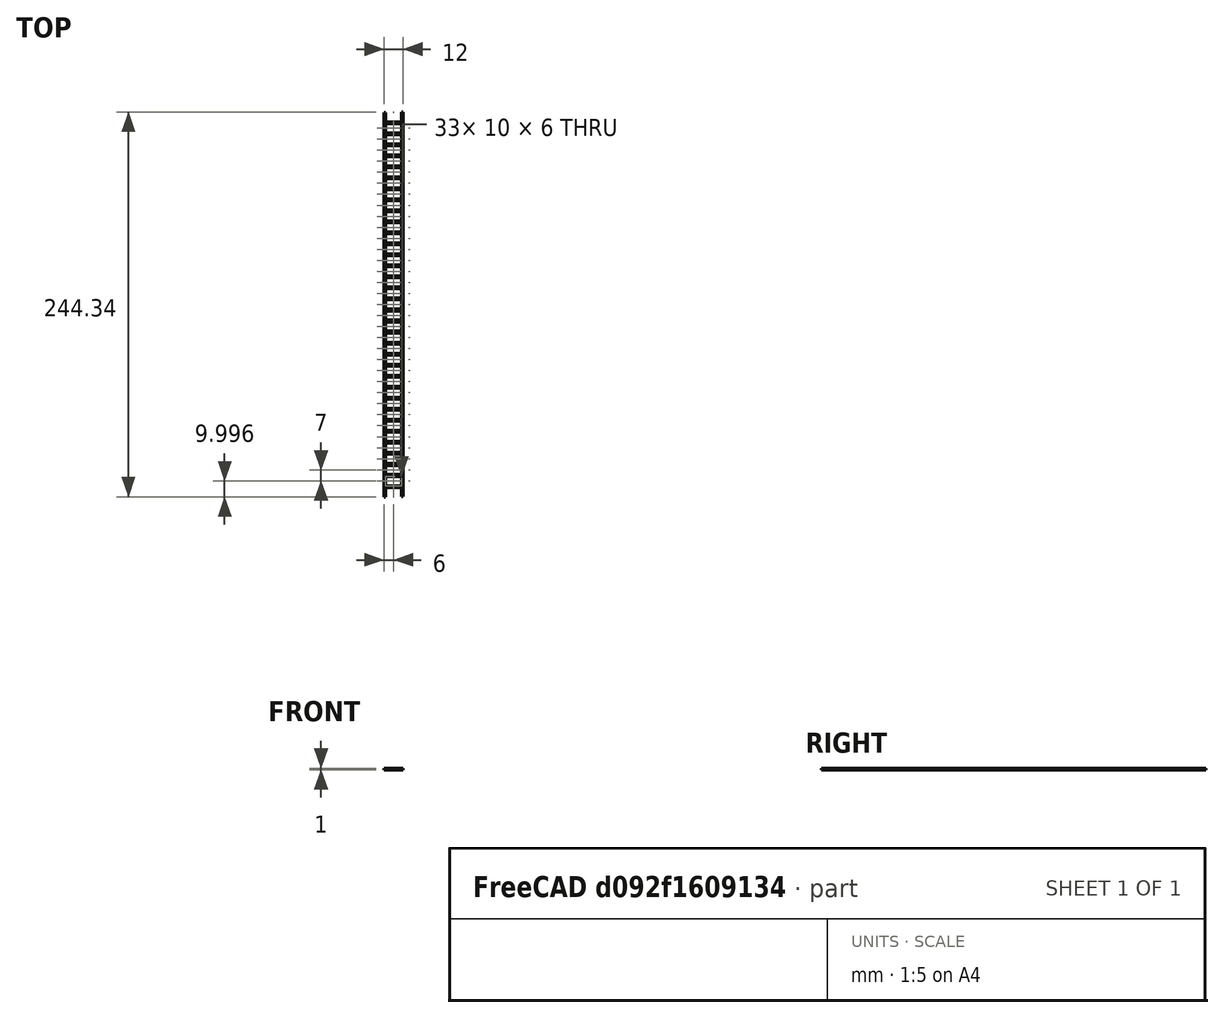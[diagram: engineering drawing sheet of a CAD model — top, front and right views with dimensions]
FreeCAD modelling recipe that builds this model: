
FCSTD DOCUMENT  (FreeCAD 1.0R39319 (Git))
Label: Ladder
License: All rights reserved
LicenseURL: http://en.wikipedia.org/wiki/All_rights_reserved
objects: Sketcher::SketchObject×2, PartDesign::Body×2, PartDesign::Pad×1
note: 9 computed .brp shape members not serialized (recipe doc carries the construction recipe); baked Part::Feature solids carry a one-line shape summary decoded from their .brp

FEATURE [Sketcher::SketchObject] Sketch
  ArcFitTolerance = 1e-06
  AttachmentSupport = -> [XY_Plane]
  FullyConstrained = true
  MakeInternals = false
  MapMode = 5
  sketch-geometry (212):
    g0: LineSegment StartX=-5 StartY=5.88621 StartZ=0 EndX=5 EndY=5.88621 EndZ=0
    g1: LineSegment StartX=-6 StartY=-0.113795 StartZ=0 EndX=-5 EndY=-0.113795 EndZ=0
    g2: LineSegment StartX=-5 StartY=5.88621 StartZ=0 EndX=-5 EndY=-0.113795 EndZ=0
    g3: LineSegment [constr] StartX=-5 StartY=6.88621 StartZ=0 EndX=-5 EndY=5.88621 EndZ=0
    g4: LineSegment StartX=5 StartY=13.8862 StartZ=0 EndX=5 EndY=19.8862 EndZ=0
    g5: LineSegment StartX=5 StartY=19.8862 StartZ=0 EndX=-5 EndY=19.8862 EndZ=0
    g6: LineSegment StartX=-5 StartY=19.8862 StartZ=0 EndX=-5 EndY=13.8862 EndZ=0
    g7: LineSegment StartX=-5 StartY=13.8862 StartZ=0 EndX=5 EndY=13.8862 EndZ=0
    g8: GeomPoint [constr] X=0 Y=16.8862 Z=0
    g9: LineSegment [constr] StartX=-5 StartY=13.8862 StartZ=0 EndX=-5 EndY=12.8862 EndZ=0
    g10: LineSegment StartX=5 StartY=21 StartZ=0 EndX=5 EndY=27 EndZ=0
    g11: LineSegment StartX=5 StartY=27 StartZ=0 EndX=-5 EndY=27 EndZ=0
    g12: LineSegment StartX=-5 StartY=27 StartZ=0 EndX=-5 EndY=21 EndZ=0
    g13: LineSegment StartX=-5 StartY=21 StartZ=0 EndX=5 EndY=21 EndZ=0
    g14: GeomPoint [constr] X=0 Y=24 Z=0
    g15: LineSegment [constr] StartX=-5 StartY=21 StartZ=0 EndX=-5 EndY=20 EndZ=0
    g16: LineSegment StartX=5 StartY=28 StartZ=0 EndX=5 EndY=34 EndZ=0
    g17: LineSegment StartX=5 StartY=34 StartZ=0 EndX=-5 EndY=34 EndZ=0
    g18: LineSegment StartX=-5 StartY=34 StartZ=0 EndX=-5 EndY=28 EndZ=0
    g19: LineSegment StartX=-5 StartY=28 StartZ=0 EndX=5 EndY=28 EndZ=0
    g20: GeomPoint [constr] X=0 Y=31 Z=0
    g21: LineSegment [constr] StartX=-5 StartY=28 StartZ=0 EndX=-5 EndY=27 EndZ=0
    g22: LineSegment StartX=5 StartY=35 StartZ=0 EndX=5 EndY=41 EndZ=0
    g23: LineSegment StartX=5 StartY=41 StartZ=0 EndX=-5 EndY=41 EndZ=0
    g24: LineSegment StartX=-5 StartY=41 StartZ=0 EndX=-5 EndY=35 EndZ=0
    g25: LineSegment StartX=-5 StartY=35 StartZ=0 EndX=5 EndY=35 EndZ=0
    g26: GeomPoint [constr] X=0 Y=38 Z=0
    g27: LineSegment [constr] StartX=-5 StartY=35 StartZ=0 EndX=-5 EndY=34 EndZ=0
    g28: LineSegment StartX=5 StartY=42 StartZ=0 EndX=5 EndY=48 EndZ=0
    g29: LineSegment StartX=5 StartY=48 StartZ=0 EndX=-5 EndY=48 EndZ=0
    g30: LineSegment StartX=-5 StartY=48 StartZ=0 EndX=-5 EndY=42 EndZ=0
    g31: LineSegment StartX=-5 StartY=42 StartZ=0 EndX=5 EndY=42 EndZ=0
    g32: GeomPoint [constr] X=0 Y=45 Z=0
    g33: LineSegment [constr] StartX=-5 StartY=42 StartZ=0 EndX=-5 EndY=41 EndZ=0
    g34: LineSegment StartX=5 StartY=49 StartZ=0 EndX=5 EndY=55 EndZ=0
    g35: LineSegment StartX=5 StartY=55 StartZ=0 EndX=-5 EndY=55 EndZ=0
    g36: LineSegment StartX=-5 StartY=55 StartZ=0 EndX=-5 EndY=49 EndZ=0
    g37: LineSegment StartX=-5 StartY=49 StartZ=0 EndX=5 EndY=49 EndZ=0
    g38: GeomPoint [constr] X=0 Y=52 Z=0
    g39: LineSegment [constr] StartX=-5 StartY=49 StartZ=0 EndX=-5 EndY=48 EndZ=0
    g40: LineSegment StartX=5 StartY=56 StartZ=0 EndX=5 EndY=62 EndZ=0
    g41: LineSegment StartX=5 StartY=62 StartZ=0 EndX=-5 EndY=62 EndZ=0
    g42: LineSegment StartX=-5 StartY=62 StartZ=0 EndX=-5 EndY=56 EndZ=0
    g43: LineSegment StartX=-5 StartY=56 StartZ=0 EndX=5 EndY=56 EndZ=0
    g44: GeomPoint [constr] X=0 Y=59 Z=0
    g45: LineSegment [constr] StartX=-5 StartY=56 StartZ=0 EndX=-5 EndY=55 EndZ=0
    g46: LineSegment StartX=5 StartY=63 StartZ=0 EndX=5 EndY=69 EndZ=0
    g47: LineSegment StartX=5 StartY=69 StartZ=0 EndX=-5 EndY=69 EndZ=0
    g48: LineSegment StartX=-5 StartY=69 StartZ=0 EndX=-5 EndY=63 EndZ=0
    g49: LineSegment StartX=-5 StartY=63 StartZ=0 EndX=5 EndY=63 EndZ=0
    g50: GeomPoint [constr] X=0 Y=66 Z=0
    g51: LineSegment [constr] StartX=-5 StartY=63 StartZ=0 EndX=-5 EndY=62 EndZ=0
    g52: LineSegment StartX=5 StartY=70 StartZ=0 EndX=5 EndY=76 EndZ=0
    g53: LineSegment StartX=5 StartY=76 StartZ=0 EndX=-5 EndY=76 EndZ=0
    g54: LineSegment StartX=-5 StartY=76 StartZ=0 EndX=-5 EndY=70 EndZ=0
    g55: LineSegment StartX=-5 StartY=70 StartZ=0 EndX=5 EndY=70 EndZ=0
    g56: GeomPoint [constr] X=0 Y=73 Z=0
    g57: LineSegment [constr] StartX=-5 StartY=70 StartZ=0 EndX=-5 EndY=69 EndZ=0
    g58: LineSegment StartX=5 StartY=77 StartZ=0 EndX=5 EndY=83 EndZ=0
    g59: LineSegment StartX=5 StartY=83 StartZ=0 EndX=-5 EndY=83 EndZ=0
    g60: LineSegment StartX=-5 StartY=83 StartZ=0 EndX=-5 EndY=77 EndZ=0
    g61: LineSegment StartX=-5 StartY=77 StartZ=0 EndX=5 EndY=77 EndZ=0
    g62: GeomPoint [constr] X=0 Y=80 Z=0
    g63: LineSegment [constr] StartX=-5 StartY=77 StartZ=0 EndX=-5 EndY=76 EndZ=0
    g64: LineSegment StartX=5 StartY=84 StartZ=0 EndX=5 EndY=90 EndZ=0
    g65: LineSegment StartX=5 StartY=90 StartZ=0 EndX=-5 EndY=90 EndZ=0
    g66: LineSegment StartX=-5 StartY=90 StartZ=0 EndX=-5 EndY=84 EndZ=0
    g67: LineSegment StartX=-5 StartY=84 StartZ=0 EndX=5 EndY=84 EndZ=0
    g68: GeomPoint [constr] X=0 Y=87 Z=0
    g69: LineSegment [constr] StartX=-5 StartY=84 StartZ=0 EndX=-5 EndY=83 EndZ=0
    g70: LineSegment StartX=5 StartY=91 StartZ=0 EndX=5 EndY=97 EndZ=0
    g71: LineSegment StartX=5 StartY=97 StartZ=0 EndX=-5 EndY=97 EndZ=0
    g72: LineSegment StartX=-5 StartY=97 StartZ=0 EndX=-5 EndY=91 EndZ=0
    g73: LineSegment StartX=-5 StartY=91 StartZ=0 EndX=5 EndY=91 EndZ=0
    g74: GeomPoint [constr] X=0 Y=94 Z=0
    g75: LineSegment [constr] StartX=-5 StartY=91 StartZ=0 EndX=-5 EndY=90 EndZ=0
    g76: LineSegment StartX=5 StartY=98 StartZ=0 EndX=5 EndY=104 EndZ=0
    g77: LineSegment StartX=5 StartY=104 StartZ=0 EndX=-5 EndY=104 EndZ=0
    g78: LineSegment StartX=-5 StartY=104 StartZ=0 EndX=-5 EndY=98 EndZ=0
    g79: LineSegment StartX=-5 StartY=98 StartZ=0 EndX=5 EndY=98 EndZ=0
    g80: GeomPoint [constr] X=0 Y=101 Z=0
    g81: LineSegment [constr] StartX=-5 StartY=98 StartZ=0 EndX=-5 EndY=97 EndZ=0
    g82: LineSegment StartX=5 StartY=105 StartZ=0 EndX=5 EndY=111 EndZ=0
    g83: LineSegment StartX=5 StartY=111 StartZ=0 EndX=-5 EndY=111 EndZ=0
    g84: LineSegment StartX=-5 StartY=111 StartZ=0 EndX=-5 EndY=105 EndZ=0
    g85: LineSegment StartX=-5 StartY=105 StartZ=0 EndX=5 EndY=105 EndZ=0
    g86: GeomPoint [constr] X=0 Y=108 Z=0
    g87: LineSegment [constr] StartX=-5 StartY=105 StartZ=0 EndX=-5 EndY=104 EndZ=0
    g88: LineSegment StartX=5 StartY=112 StartZ=0 EndX=5 EndY=118 EndZ=0
    g89: LineSegment StartX=5 StartY=118 StartZ=0 EndX=-5 EndY=118 EndZ=0
    g90: LineSegment StartX=-5 StartY=118 StartZ=0 EndX=-5 EndY=112 EndZ=0
    g91: LineSegment StartX=-5 StartY=112 StartZ=0 EndX=5 EndY=112 EndZ=0
    g92: GeomPoint [constr] X=0 Y=115 Z=0
    g93: LineSegment [constr] StartX=-5 StartY=112 StartZ=0 EndX=-5 EndY=111 EndZ=0
    g94: LineSegment StartX=5 StartY=119 StartZ=0 EndX=5 EndY=125 EndZ=0
    g95: LineSegment StartX=5 StartY=125 StartZ=0 EndX=-5 EndY=125 EndZ=0
    g96: LineSegment StartX=-5 StartY=125 StartZ=0 EndX=-5 EndY=119 EndZ=0
    g97: LineSegment StartX=-5 StartY=119 StartZ=0 EndX=5 EndY=119 EndZ=0
    g98: GeomPoint [constr] X=0 Y=122 Z=0
    g99: LineSegment [constr] StartX=-5 StartY=119 StartZ=0 EndX=-5 EndY=118 EndZ=0
    g100: LineSegment StartX=5 StartY=126 StartZ=0 EndX=5 EndY=132 EndZ=0
    g101: LineSegment StartX=5 StartY=132 StartZ=0 EndX=-5 EndY=132 EndZ=0
    g102: LineSegment StartX=-5 StartY=132 StartZ=0 EndX=-5 EndY=126 EndZ=0
    g103: LineSegment StartX=-5 StartY=126 StartZ=0 EndX=5 EndY=126 EndZ=0
    g104: GeomPoint [constr] X=0 Y=129 Z=0
    g105: LineSegment [constr] StartX=-5 StartY=126 StartZ=0 EndX=-5 EndY=125 EndZ=0
    g106: LineSegment StartX=5 StartY=133 StartZ=0 EndX=5 EndY=139 EndZ=0
    g107: LineSegment StartX=5 StartY=139 StartZ=0 EndX=-5 EndY=139 EndZ=0
    g108: LineSegment StartX=-5 StartY=139 StartZ=0 EndX=-5 EndY=133 EndZ=0
    g109: LineSegment StartX=-5 StartY=133 StartZ=0 EndX=5 EndY=133 EndZ=0
    g110: GeomPoint [constr] X=0 Y=136 Z=0
    g111: LineSegment [constr] StartX=-5 StartY=133 StartZ=0 EndX=-5 EndY=132 EndZ=0
    g112: LineSegment StartX=5 StartY=140 StartZ=0 EndX=5 EndY=146 EndZ=0
    g113: LineSegment StartX=5 StartY=146 StartZ=0 EndX=-5 EndY=146 EndZ=0
    g114: LineSegment StartX=-5 StartY=146 StartZ=0 EndX=-5 EndY=140 EndZ=0
    g115: LineSegment StartX=-5 StartY=140 StartZ=0 EndX=5 EndY=140 EndZ=0
    g116: GeomPoint [constr] X=0 Y=143 Z=0
    g117: LineSegment [constr] StartX=-5 StartY=140 StartZ=0 EndX=-5 EndY=139 EndZ=0
    g118: LineSegment StartX=5 StartY=147 StartZ=0 EndX=5 EndY=153 EndZ=0
    g119: LineSegment StartX=5 StartY=153 StartZ=0 EndX=-5 EndY=153 EndZ=0
    g120: LineSegment StartX=-5 StartY=153 StartZ=0 EndX=-5 EndY=147 EndZ=0
    g121: LineSegment StartX=-5 StartY=147 StartZ=0 EndX=5 EndY=147 EndZ=0
    g122: GeomPoint [constr] X=0 Y=150 Z=0
    g123: LineSegment [constr] StartX=-5 StartY=147 StartZ=0 EndX=-5 EndY=146 EndZ=0
    g124: LineSegment StartX=5 StartY=154 StartZ=0 EndX=5 EndY=160 EndZ=0
    g125: LineSegment StartX=5 StartY=160 StartZ=0 EndX=-5 EndY=160 EndZ=0
    g126: LineSegment StartX=-5 StartY=160 StartZ=0 EndX=-5 EndY=154 EndZ=0
    g127: LineSegment StartX=-5 StartY=154 StartZ=0 EndX=5 EndY=154 EndZ=0
    g128: GeomPoint [constr] X=0 Y=157 Z=0
    g129: LineSegment [constr] StartX=-5 StartY=154 StartZ=0 EndX=-5 EndY=153 EndZ=0
    g130: LineSegment StartX=5 StartY=161 StartZ=0 EndX=5 EndY=167 EndZ=0
    g131: LineSegment StartX=5 StartY=167 StartZ=0 EndX=-5 EndY=167 EndZ=0
    g132: LineSegment StartX=-5 StartY=167 StartZ=0 EndX=-5 EndY=161 EndZ=0
    g133: LineSegment StartX=-5 StartY=161 StartZ=0 EndX=5 EndY=161 EndZ=0
    g134: GeomPoint [constr] X=0 Y=164 Z=0
    g135: LineSegment [constr] StartX=-5 StartY=161 StartZ=0 EndX=-5 EndY=160 EndZ=0
    g136: LineSegment StartX=5 StartY=168 StartZ=0 EndX=5 EndY=174 EndZ=0
    g137: LineSegment StartX=5 StartY=174 StartZ=0 EndX=-5 EndY=174 EndZ=0
    g138: LineSegment StartX=-5 StartY=174 StartZ=0 EndX=-5 EndY=168 EndZ=0
    g139: LineSegment StartX=-5 StartY=168 StartZ=0 EndX=5 EndY=168 EndZ=0
    g140: GeomPoint [constr] X=0 Y=171 Z=0
    g141: LineSegment [constr] StartX=-5 StartY=168 StartZ=0 EndX=-5 EndY=167 EndZ=0
    g142: LineSegment StartX=5 StartY=175 StartZ=0 EndX=5 EndY=181 EndZ=0
    g143: LineSegment StartX=5 StartY=181 StartZ=0 EndX=-5 EndY=181 EndZ=0
    g144: LineSegment StartX=-5 StartY=181 StartZ=0 EndX=-5 EndY=175 EndZ=0
    g145: LineSegment StartX=-5 StartY=175 StartZ=0 EndX=5 EndY=175 EndZ=0
    g146: GeomPoint [constr] X=0 Y=178 Z=0
    g147: LineSegment [constr] StartX=-5 StartY=175 StartZ=0 EndX=-5 EndY=174 EndZ=0
    g148: LineSegment StartX=5 StartY=182 StartZ=0 EndX=5 EndY=188 EndZ=0
    g149: LineSegment StartX=5 StartY=188 StartZ=0 EndX=-5 EndY=188 EndZ=0
    g150: LineSegment StartX=-5 StartY=188 StartZ=0 EndX=-5 EndY=182 EndZ=0
    g151: LineSegment StartX=-5 StartY=182 StartZ=0 EndX=5 EndY=182 EndZ=0
    g152: GeomPoint [constr] X=0 Y=185 Z=0
    g153: LineSegment [constr] StartX=-5 StartY=182 StartZ=0 EndX=-5 EndY=181 EndZ=0
    g154: LineSegment StartX=5 StartY=189 StartZ=0 EndX=5 EndY=195 EndZ=0
    g155: LineSegment StartX=5 StartY=195 StartZ=0 EndX=-5 EndY=195 EndZ=0
    g156: LineSegment StartX=-5 StartY=195 StartZ=0 EndX=-5 EndY=189 EndZ=0
    g157: LineSegment StartX=-5 StartY=189 StartZ=0 EndX=5 EndY=189 EndZ=0
    g158: GeomPoint [constr] X=0 Y=192 Z=0
    g159: LineSegment [constr] StartX=-5 StartY=189 StartZ=0 EndX=-5 EndY=188 EndZ=0
    g160: LineSegment StartX=5 StartY=196 StartZ=0 EndX=5 EndY=202 EndZ=0
    g161: LineSegment StartX=5 StartY=202 StartZ=0 EndX=-5 EndY=202 EndZ=0
    g162: LineSegment StartX=-5 StartY=202 StartZ=0 EndX=-5 EndY=196 EndZ=0
    g163: LineSegment StartX=-5 StartY=196 StartZ=0 EndX=5 EndY=196 EndZ=0
    g164: GeomPoint [constr] X=0 Y=199 Z=0
    g165: LineSegment [constr] StartX=-5 StartY=196 StartZ=0 EndX=-5 EndY=195 EndZ=0
    g166: LineSegment StartX=5 StartY=203 StartZ=0 EndX=5 EndY=209 EndZ=0
    g167: LineSegment StartX=5 StartY=209 StartZ=0 EndX=-5 EndY=209 EndZ=0
    g168: LineSegment StartX=-5 StartY=209 StartZ=0 EndX=-5 EndY=203 EndZ=0
    g169: LineSegment StartX=-5 StartY=203 StartZ=0 EndX=5 EndY=203 EndZ=0
    g170: GeomPoint [constr] X=0 Y=206 Z=0
    g171: LineSegment [constr] StartX=-5 StartY=203 StartZ=0 EndX=-5 EndY=202 EndZ=0
    g172: LineSegment StartX=5 StartY=210 StartZ=0 EndX=5 EndY=216 EndZ=0
    g173: LineSegment StartX=5 StartY=216 StartZ=0 EndX=-5 EndY=216 EndZ=0
    g174: LineSegment StartX=-5 StartY=216 StartZ=0 EndX=-5 EndY=210 EndZ=0
    g175: LineSegment StartX=-5 StartY=210 StartZ=0 EndX=5 EndY=210 EndZ=0
    g176: GeomPoint [constr] X=0 Y=213 Z=0
    g177: LineSegment [constr] StartX=-5 StartY=210 StartZ=0 EndX=-5 EndY=209 EndZ=0
    g178: LineSegment StartX=5 StartY=217 StartZ=0 EndX=5 EndY=223 EndZ=0
    g179: LineSegment StartX=5 StartY=223 StartZ=0 EndX=-5 EndY=223 EndZ=0
    g180: LineSegment StartX=-5 StartY=223 StartZ=0 EndX=-5 EndY=217 EndZ=0
    g181: LineSegment StartX=-5 StartY=217 StartZ=0 EndX=5 EndY=217 EndZ=0
    g182: GeomPoint [constr] X=0 Y=220 Z=0
    g183: LineSegment [constr] StartX=-5 StartY=217 StartZ=0 EndX=-5 EndY=216 EndZ=0
    g184: LineSegment StartX=5 StartY=224 StartZ=0 EndX=5 EndY=230 EndZ=0
    g185: LineSegment StartX=5 StartY=230 StartZ=0 EndX=-5 EndY=230 EndZ=0
    g186: LineSegment StartX=-5 StartY=230 StartZ=0 EndX=-5 EndY=224 EndZ=0
    g187: LineSegment StartX=-5 StartY=224 StartZ=0 EndX=5 EndY=224 EndZ=0
    g188: GeomPoint [constr] X=0 Y=227 Z=0
    g189: LineSegment [constr] StartX=-5 StartY=224 StartZ=0 EndX=-5 EndY=223 EndZ=0
    g190: LineSegment StartX=5 StartY=231 StartZ=0 EndX=5 EndY=237 EndZ=0
    g191: LineSegment StartX=5 StartY=237 StartZ=0 EndX=-5 EndY=237 EndZ=0
    g192: LineSegment StartX=-5 StartY=237 StartZ=0 EndX=-5 EndY=231 EndZ=0
    g193: LineSegment StartX=-5 StartY=231 StartZ=0 EndX=5 EndY=231 EndZ=0
    g194: GeomPoint [constr] X=0 Y=234 Z=0
    g195: LineSegment [constr] StartX=-5 StartY=231 StartZ=0 EndX=-5 EndY=230 EndZ=0
    g196: LineSegment StartX=5 StartY=238 StartZ=0 EndX=5 EndY=244.228 EndZ=0
    g197: LineSegment StartX=-5 StartY=244 StartZ=0 EndX=-5 EndY=238 EndZ=0
    g198: LineSegment StartX=-5 StartY=238 StartZ=0 EndX=5 EndY=238 EndZ=0
    g199: GeomPoint [constr] X=1.09e-14 Y=241 Z=0
    g200: LineSegment [constr] StartX=-5 StartY=238 StartZ=0 EndX=-5 EndY=237 EndZ=0
    g201: LineSegment StartX=-6 StartY=244 StartZ=0 EndX=-5 EndY=244 EndZ=0
    g202: LineSegment StartX=5 StartY=244.228 StartZ=0 EndX=6 EndY=244.228 EndZ=0
    g203: LineSegment StartX=6 StartY=244.228 StartZ=0 EndX=6 EndY=0.113795 EndZ=0
    g204: LineSegment StartX=5 StartY=5.88621 StartZ=0 EndX=5 EndY=0.113795 EndZ=0
    g205: LineSegment StartX=5 StartY=0.113795 StartZ=0 EndX=6 EndY=0.113795 EndZ=0
    g206: LineSegment StartX=-5 StartY=6.88621 StartZ=0 EndX=5 EndY=6.88621 EndZ=0
    g207: LineSegment StartX=5 StartY=6.88621 StartZ=0 EndX=5 EndY=12.8862 EndZ=0
    g208: LineSegment StartX=5 StartY=12.8862 StartZ=0 EndX=-5 EndY=12.8862 EndZ=0
    g209: LineSegment StartX=-5 StartY=12.8862 StartZ=0 EndX=-5 EndY=6.88621 EndZ=0
    g210: GeomPoint [constr] X=0 Y=9.88621 Z=0
    g211: LineSegment StartX=-6 StartY=244 StartZ=0 EndX=-6 EndY=-0.113795 EndZ=0
  constraints (631):
    c: Horizontal(g0)
    c: DistanceY(g1,g0) = 6
    c: DistanceX(g0,g0) = 10
    c: DistanceX(g1,g1) = 1
    c: Coincident(g2,g0)
    c: Coincident(g3,g0)
    c: DistanceY(g3,g3) = 1
    c: Coincident(g1,g2)
    c: Vertical(g2)
    c: Horizontal(g1)
    c: Coincident(g4,g5)
    c: Coincident(g10,g11)
    c: Coincident(g16,g17)
    c: Coincident(g22,g23)
    c: Coincident(g28,g29)
    c: Coincident(g34,g35)
    c: Coincident(g40,g41)
    c: Coincident(g46,g47)
    c: Coincident(g52,g53)
    c: Coincident(g58,g59)
    c: Coincident(g64,g65)
    c: Coincident(g70,g71)
    c: Coincident(g76,g77)
    c: Coincident(g82,g83)
    c: Coincident(g88,g89)
    c: Coincident(g94,g95)
    c: Coincident(g100,g101)
    c: Coincident(g106,g107)
    c: Coincident(g112,g113)
    c: Coincident(g118,g119)
    c: Coincident(g124,g125)
    c: Coincident(g130,g131)
    c: Coincident(g136,g137)
    c: Coincident(g142,g143)
    c: Coincident(g148,g149)
    c: Coincident(g154,g155)
    c: Coincident(g160,g161)
    c: Coincident(g166,g167)
    c: Coincident(g172,g173)
    c: Coincident(g178,g179)
    c: Coincident(g5,g6)
    c: Coincident(g11,g12)
    c: Coincident(g17,g18)
    c: Coincident(g23,g24)
    c: Coincident(g29,g30)
    c: Coincident(g35,g36)
    c: Coincident(g41,g42)
    c: Coincident(g47,g48)
    c: Coincident(g53,g54)
    c: Coincident(g59,g60)
    c: Coincident(g65,g66)
    c: Coincident(g71,g72)
    c: Coincident(g77,g78)
    c: Coincident(g83,g84)
    c: Coincident(g89,g90)
    c: Coincident(g95,g96)
    c: Coincident(g101,g102)
    c: Coincident(g107,g108)
    c: Coincident(g113,g114)
    c: Coincident(g119,g120)
    c: Coincident(g125,g126)
    c: Coincident(g131,g132)
    c: Coincident(g137,g138)
    c: Coincident(g143,g144)
    c: Coincident(g149,g150)
    c: Coincident(g155,g156)
    c: Coincident(g161,g162)
    c: Coincident(g167,g168)
    c: Coincident(g173,g174)
    c: Coincident(g179,g180)
    c: Coincident(g6,g7)
    c: Coincident(g12,g13)
    c: Coincident(g18,g19)
    c: Coincident(g24,g25)
    c: Coincident(g30,g31)
    c: Coincident(g36,g37)
    c: Coincident(g42,g43)
    c: Coincident(g48,g49)
    c: Coincident(g54,g55)
    c: Coincident(g60,g61)
    c: Coincident(g66,g67)
    c: Coincident(g72,g73)
    c: Coincident(g78,g79)
    c: Coincident(g84,g85)
    c: Coincident(g90,g91)
    c: Coincident(g96,g97)
    c: Coincident(g102,g103)
    c: Coincident(g108,g109)
    c: Coincident(g114,g115)
    c: Coincident(g120,g121)
    c: Coincident(g126,g127)
    c: Coincident(g132,g133)
    c: Coincident(g138,g139)
    c: Coincident(g144,g145)
    c: Coincident(g150,g151)
    c: Coincident(g156,g157)
    c: Coincident(g162,g163)
    c: Coincident(g168,g169)
    c: Coincident(g174,g175)
    c: Coincident(g180,g181)
    c: Coincident(g7,g4)
    c: Coincident(g13,g10)
    c: Coincident(g19,g16)
    c: Coincident(g25,g22)
    c: Coincident(g31,g28)
    c: Coincident(g37,g34)
    c: Coincident(g43,g40)
    c: Coincident(g49,g46)
    c: Coincident(g55,g52)
    c: Coincident(g61,g58)
    c: Coincident(g67,g64)
    c: Coincident(g73,g70)
    c: Coincident(g79,g76)
    c: Coincident(g85,g82)
    c: Coincident(g91,g88)
    c: Coincident(g97,g94)
    c: Coincident(g103,g100)
    c: Coincident(g109,g106)
    c: Coincident(g115,g112)
    c: Coincident(g121,g118)
    c: Coincident(g127,g124)
    c: Coincident(g133,g130)
    c: Coincident(g139,g136)
    c: Coincident(g145,g142)
    c: Coincident(g151,g148)
    c: Coincident(g157,g154)
    c: Coincident(g163,g160)
    c: Coincident(g169,g166)
    c: Coincident(g175,g172)
    c: Coincident(g181,g178)
    c: Vertical(g4)
    c: Vertical(g10)
    c: Vertical(g16)
    c: Vertical(g22)
    c: Vertical(g28)
    c: Vertical(g34)
    c: Vertical(g40)
    c: Vertical(g46)
    c: Vertical(g52)
    c: Vertical(g58)
    c: Vertical(g64)
    c: Vertical(g70)
    c: Vertical(g76)
    c: Vertical(g82)
    c: Vertical(g88)
    c: Vertical(g94)
    c: Vertical(g100)
    c: Vertical(g106)
    c: Vertical(g112)
    c: Vertical(g118)
    c: Vertical(g124)
    c: Vertical(g130)
    c: Vertical(g136)
    c: Vertical(g142)
    c: Vertical(g148)
    c: Vertical(g154)
    c: Vertical(g160)
    c: Vertical(g166)
    c: Vertical(g172)
    c: Vertical(g178)
    c: Vertical(g6)
    c: Vertical(g12)
    c: Vertical(g18)
    c: Vertical(g24)
    c: Vertical(g30)
    c: Vertical(g36)
    c: Vertical(g42)
    c: Vertical(g48)
    c: Vertical(g54)
    c: Vertical(g60)
    c: Vertical(g66)
    c: Vertical(g72)
    c: Vertical(g78)
    c: Vertical(g84)
    c: Vertical(g90)
    c: Vertical(g96)
    c: Vertical(g102)
    c: Vertical(g108)
    c: Vertical(g114)
    c: Vertical(g120)
    c: Vertical(g126)
    c: Vertical(g132)
    c: Vertical(g138)
    c: Vertical(g144)
    c: Vertical(g150)
    c: Vertical(g156)
    c: Vertical(g162)
    c: Vertical(g168)
    c: Vertical(g174)
    c: Vertical(g180)
    c: Horizontal(g5)
    c: Horizontal(g11)
    c: Horizontal(g17)
    c: Horizontal(g23)
    c: Horizontal(g29)
    c: Horizontal(g35)
    c: Horizontal(g41)
    c: Horizontal(g47)
    c: Horizontal(g53)
    c: Horizontal(g59)
    c: Horizontal(g65)
    c: Horizontal(g71)
    c: Horizontal(g77)
    c: Horizontal(g83)
    c: Horizontal(g89)
    c: Horizontal(g95)
    c: Horizontal(g101)
    c: Horizontal(g107)
    c: Horizontal(g113)
    c: Horizontal(g119)
    c: Horizontal(g125)
    c: Horizontal(g131)
    c: Horizontal(g137)
    c: Horizontal(g143)
    c: Horizontal(g149)
    c: Horizontal(g155)
    c: Horizontal(g161)
    c: Horizontal(g167)
    c: Horizontal(g173)
    c: Horizontal(g179)
    c: Horizontal(g7)
    c: Horizontal(g13)
    c: Horizontal(g19)
    c: Horizontal(g25)
    c: Horizontal(g31)
    c: Horizontal(g37)
    c: Horizontal(g43)
    c: Horizontal(g49)
    c: Horizontal(g55)
    c: Horizontal(g61)
    c: Horizontal(g67)
    c: Horizontal(g73)
    c: Horizontal(g79)
    c: Horizontal(g85)
    c: Horizontal(g91)
    c: Horizontal(g97)
    c: Horizontal(g103)
    c: Horizontal(g109)
    c: Horizontal(g115)
    c: Horizontal(g121)
    c: Horizontal(g127)
    c: Horizontal(g133)
    c: Horizontal(g139)
    c: Horizontal(g145)
    c: Horizontal(g151)
    c: Horizontal(g157)
    c: Horizontal(g163)
    c: Horizontal(g169)
    c: Horizontal(g175)
    c: Horizontal(g181)
    c: Symmetric(g6,g4,g8)
    c: Symmetric(g12,g10,g14)
    c: Symmetric(g18,g16,g20)
    c: Symmetric(g24,g22,g26)
    c: Symmetric(g30,g28,g32)
    c: Symmetric(g36,g34,g38)
    c: Symmetric(g42,g40,g44)
    c: Symmetric(g48,g46,g50)
    c: Symmetric(g54,g52,g56)
    c: Symmetric(g60,g58,g62)
    c: Symmetric(g66,g64,g68)
    c: Symmetric(g72,g70,g74)
    c: Symmetric(g78,g76,g80)
    c: Symmetric(g84,g82,g86)
    c: Symmetric(g90,g88,g92)
    c: Symmetric(g96,g94,g98)
    c: Symmetric(g102,g100,g104)
    c: Symmetric(g108,g106,g110)
    c: Symmetric(g114,g112,g116)
    c: Symmetric(g120,g118,g122)
    c: Symmetric(g126,g124,g128)
    c: Symmetric(g132,g130,g134)
    c: Symmetric(g138,g136,g140)
    c: Symmetric(g144,g142,g146)
    c: Symmetric(g150,g148,g152)
    c: Symmetric(g156,g154,g158)
    c: Symmetric(g162,g160,g164)
    c: Symmetric(g168,g166,g170)
    c: Symmetric(g174,g172,g176)
    c: Symmetric(g180,g178,g182)
    c: DistanceY(g6,g6) = 6
    c: DistanceY(g12,g12) = 6
    c: DistanceY(g18,g18) = 6
    c: DistanceY(g24,g24) = 6
    c: DistanceY(g30,g30) = 6
    c: DistanceY(g36,g36) = 6
    c: DistanceY(g42,g42) = 6
    c: DistanceY(g48,g48) = 6
    c: DistanceY(g54,g54) = 6
    c: DistanceY(g60,g60) = 6
    c: DistanceY(g66,g66) = 6
    c: DistanceY(g72,g72) = 6
    c: DistanceY(g78,g78) = 6
    c: DistanceY(g84,g84) = 6
    c: DistanceY(g90,g90) = 6
    c: DistanceY(g96,g96) = 6
    c: DistanceY(g102,g102) = 6
    c: DistanceY(g108,g108) = 6
    c: DistanceY(g114,g114) = 6
    c: DistanceY(g120,g120) = 6
    c: DistanceY(g126,g126) = 6
    c: DistanceY(g132,g132) = 6
    c: DistanceY(g138,g138) = 6
    c: DistanceY(g144,g144) = 6
    c: DistanceY(g150,g150) = 6
    c: DistanceY(g156,g156) = 6
    c: DistanceY(g162,g162) = 6
    c: DistanceY(g168,g168) = 6
    c: DistanceY(g174,g174) = 6
    c: DistanceY(g180,g180) = 6
    c: Coincident(g9,g6)
    c: Coincident(g15,g12)
    c: Coincident(g21,g18)
    c: Coincident(g27,g24)
    c: Coincident(g33,g30)
    c: Coincident(g39,g36)
    c: Coincident(g45,g42)
    c: Coincident(g51,g48)
    c: Coincident(g57,g54)
    c: Coincident(g63,g60)
    c: Coincident(g69,g66)
    c: Coincident(g75,g72)
    c: Coincident(g81,g78)
    c: Coincident(g87,g84)
    c: Coincident(g93,g90)
    c: Coincident(g99,g96)
    c: Coincident(g105,g102)
    c: Coincident(g111,g108)
    c: Coincident(g117,g114)
    c: Coincident(g123,g120)
    c: Coincident(g129,g126)
    c: Coincident(g135,g132)
    c: Coincident(g141,g138)
    c: Coincident(g147,g144)
    c: Coincident(g153,g150)
    c: Coincident(g159,g156)
    c: Coincident(g165,g162)
    c: Coincident(g171,g168)
    c: Coincident(g177,g174)
    c: Coincident(g183,g180)
    c: DistanceX(g5,g5) = 10
    c: DistanceX(g11,g11) = 10
    c: DistanceX(g17,g17) = 10
    c: DistanceX(g23,g23) = 10
    c: DistanceX(g29,g29) = 10
    c: DistanceX(g35,g35) = 10
    c: DistanceX(g41,g41) = 10
    c: DistanceX(g47,g47) = 10
    c: DistanceX(g53,g53) = 10
    c: DistanceX(g59,g59) = 10
    c: DistanceX(g65,g65) = 10
    c: DistanceX(g71,g71) = 10
    c: DistanceX(g77,g77) = 10
    c: DistanceX(g83,g83) = 10
    c: DistanceX(g89,g89) = 10
    c: DistanceX(g95,g95) = 10
    c: DistanceX(g101,g101) = 10
    c: DistanceX(g107,g107) = 10
    c: DistanceX(g113,g113) = 10
    c: DistanceX(g119,g119) = 10
    c: DistanceX(g125,g125) = 10
    c: DistanceX(g131,g131) = 10
    c: DistanceX(g137,g137) = 10
    c: DistanceX(g143,g143) = 10
    c: DistanceX(g149,g149) = 10
    c: DistanceX(g155,g155) = 10
    c: DistanceX(g161,g161) = 10
    c: DistanceX(g167,g167) = 10
    c: DistanceX(g173,g173) = 10
    c: DistanceX(g179,g179) = 10
    c: DistanceY(g9,g9) = 1
    c: DistanceY(g15,g15) = 1
    c: DistanceY(g21,g21) = 1
    c: DistanceY(g27,g27) = 1
    c: DistanceY(g33,g33) = 1
    c: DistanceY(g39,g39) = 1
    c: DistanceY(g45,g45) = 1
    c: DistanceY(g51,g51) = 1
    c: DistanceY(g57,g57) = 1
    c: DistanceY(g63,g63) = 1
    c: DistanceY(g69,g69) = 1
    c: DistanceY(g75,g75) = 1
    c: DistanceY(g81,g81) = 1
    c: DistanceY(g87,g87) = 1
    c: DistanceY(g93,g93) = 1
    c: DistanceY(g99,g99) = 1
    c: DistanceY(g105,g105) = 1
    c: DistanceY(g111,g111) = 1
    c: DistanceY(g117,g117) = 1
    c: DistanceY(g123,g123) = 1
    c: DistanceY(g129,g129) = 1
    c: DistanceY(g135,g135) = 1
    c: DistanceY(g141,g141) = 1
    c: DistanceY(g147,g147) = 1
    c: DistanceY(g153,g153) = 1
    c: DistanceY(g159,g159) = 1
    c: DistanceY(g165,g165) = 1
    c: DistanceY(g171,g171) = 1
    c: DistanceY(g177,g177) = 1
    c: DistanceY(g183,g183) = 1
    c: Block(g5)
    c: Block(g11)
    c: Block(g17)
    c: Block(g23)
    c: Block(g29)
    c: Block(g35)
    c: Block(g41)
    c: Block(g47)
    c: Block(g53)
    c: Block(g59)
    c: Block(g65)
    c: Block(g71)
    c: Block(g77)
    c: Block(g83)
    c: Block(g89)
    c: Block(g95)
    c: Block(g101)
    c: Block(g107)
    c: Block(g113)
    c: Block(g119)
    c: Block(g125)
    c: Block(g131)
    c: Block(g137)
    c: Block(g143)
    c: Block(g149)
    c: Block(g155)
    c: Block(g161)
    c: Block(g167)
    c: Block(g173)
    c: Block(g179)
    c: Block(g6)
    c: Block(g12)
    c: Block(g18)
    c: Block(g24)
    c: Block(g30)
    c: Block(g36)
    c: Block(g42)
    c: Block(g48)
    c: Block(g54)
    c: Block(g60)
    c: Block(g66)
    c: Block(g72)
    c: Block(g78)
    c: Block(g84)
    c: Block(g90)
    c: Block(g96)
    c: Block(g102)
    c: Block(g108)
    c: Block(g114)
    c: Block(g120)
    c: Block(g126)
    c: Block(g132)
    c: Block(g138)
    c: Block(g144)
    c: Block(g150)
    c: Block(g156)
    c: Block(g162)
    c: Block(g168)
    c: Block(g174)
    c: Block(g180)
    c: Block(g7)
    c: Block(g13)
    c: Block(g19)
    c: Block(g25)
    c: Block(g31)
    c: Block(g37)
    c: Block(g43)
    c: Block(g49)
    c: Block(g55)
    c: Block(g61)
    c: Block(g67)
    c: Block(g73)
    c: Block(g79)
    c: Block(g85)
    c: Block(g91)
    c: Block(g97)
    c: Block(g103)
    c: Block(g109)
    c: Block(g115)
    c: Block(g121)
    c: Block(g127)
    c: Block(g133)
    c: Block(g139)
    c: Block(g145)
    c: Block(g151)
    c: Block(g157)
    c: Block(g163)
    c: Block(g169)
    c: Block(g175)
    c: Block(g181)
    c: Block(g4)
    c: Block(g10)
    c: Block(g16)
    c: Block(g22)
    c: Block(g28)
    c: Block(g34)
    c: Block(g40)
    c: Block(g46)
    c: Block(g52)
    c: Block(g58)
    c: Block(g64)
    c: Block(g70)
    c: Block(g76)
    c: Block(g82)
    c: Block(g88)
    c: Block(g94)
    c: Block(g100)
    c: Block(g106)
    c: Block(g112)
    c: Block(g118)
    c: Block(g124)
    c: Block(g130)
    c: Block(g136)
    c: Block(g142)
    c: Block(g148)
    c: Block(g154)
    c: Block(g160)
    c: Block(g166)
    c: Block(g172)
    c: Block(g178)
    c: Block(g9)
    c: Block(g15)
    c: Block(g21)
    c: Block(g27)
    c: Block(g33)
    c: Block(g39)
    c: Block(g45)
    c: Block(g51)
    c: Block(g57)
    c: Block(g63)
    c: Block(g69)
    c: Block(g75)
    c: Block(g81)
    c: Block(g87)
    c: Block(g93)
    c: Block(g99)
    c: Block(g105)
    c: Block(g111)
    c: Block(g117)
    c: Block(g123)
    c: Block(g129)
    c: Block(g135)
    c: Block(g141)
    c: Block(g147)
    c: Block(g153)
    c: Block(g159)
    c: Block(g165)
    c: Block(g171)
    c: Block(g177)
    c: Block(g183)
    c: Coincident(g184,g185)
    c: Coincident(g190,g191)
    c: Coincident(g185,g186)
    c: Coincident(g191,g192)
    c: Coincident(g186,g187)
    c: Coincident(g192,g193)
    c: Coincident(g197,g198)
    c: Coincident(g187,g184)
    c: Coincident(g193,g190)
    c: Coincident(g198,g196)
    c: Vertical(g184)
    c: Vertical(g190)
    c: Vertical(g196)
    c: Vertical(g186)
    c: Vertical(g192)
    c: Vertical(g197)
    c: Horizontal(g185)
    c: Horizontal(g191)
    c: Horizontal(g187)
    c: Horizontal(g193)
    c: Horizontal(g198)
    c: Symmetric(g186,g184,g188)
    c: Symmetric(g192,g190,g194)
    c: Symmetric(g197,g196,g199)
    c: DistanceY(g186,g186) = 6
    c: DistanceY(g192,g192) = 6
    c: DistanceY(g197,g197) = 6
    c: Coincident(g189,g186)
    c: Coincident(g195,g192)
    c: Coincident(g200,g197)
    c: DistanceX(g185,g185) = 10
    c: DistanceX(g191,g191) = 10
    c: DistanceX(g197,g196) = 10
    c: DistanceY(g189,g189) = 1
    c: DistanceY(g195,g195) = 1
    c: DistanceY(g200,g200) = 1
    c: Block(g185)
    c: Block(g191)
    c: Block(g186)
    c: Block(g192)
    c: Block(g197)
    c: Block(g187)
    c: Block(g193)
    c: Block(g198)
    c: Block(g184)
    c: Block(g190)
    c: Block(g196)
    c: Block(g189)
    c: Block(g195)
    c: Block(g200)
    c: Coincident(g201,g197)
    c: Horizontal(g201)
    c: Coincident(g196,g202)
    c: Horizontal(g202)
    c: Coincident(g202,g203)
    c: Vertical(g203)
    c: Equal(g202,g201)
    c: Coincident(g0,g204)
    c: Coincident(g204,g205)
    c: Coincident(g205,g203)
    c: Horizontal(g205)
    c: Vertical(g204)
    c: Coincident(g206,g207)
    c: Coincident(g207,g208)
    c: Coincident(g208,g209)
    c: Coincident(g209,g206)
    c: Horizontal(g206)
    c: Horizontal(g208)
    c: Vertical(g207)
    c: Vertical(g209)
    c: Symmetric(g208,g206,g210)
    c: PointOnObject(g210,g-2)
    c: Equal(g208,g7)
    c: Equal(g4,g207)
    c: Coincident(g208,g9)
    c: Coincident(g3,g206)
    c: Symmetric(g204,g1,g-1)
    c: Vertical(g211)
    c: Equal(g211,g203)
    c: Coincident(g211,g1)
    c: Coincident(g211,g201)
FEATURE [PartDesign::Pad] Pad
  Direction = (0,0,1)
  Length = 1
  Length2 = 10
  Profile = -> Sketch
  ReferenceAxis = -> Sketch [N_Axis]
  Refine = true
  Suppressed = false
  Type = 0
FEATURE [PartDesign::Body] Body
  AllowCompound = true
  Group = -> [Sketch,Pad]
  Origin = -> Origin
  Tip = -> Pad
FEATURE [Sketcher::SketchObject] Sketch001
  ArcFitTolerance = 1e-06
  AttachmentSupport = -> [XY_Plane001]
  FullyConstrained = false
  MakeInternals = false
  MapMode = 5
  sketch-geometry (11):
    g0: LineSegment StartX=-37.6711 StartY=0 StartZ=0 EndX=37.6711 EndY=0 EndZ=0
    g1: LineSegment StartX=37.6711 StartY=0 StartZ=0 EndX=22.7716 EndY=181.451 EndZ=0
    g2: LineSegment StartX=22.7716 StartY=181.451 StartZ=0 EndX=-22.7716 EndY=181.451 EndZ=0
    g3: LineSegment StartX=-22.7716 StartY=181.451 StartZ=0 EndX=-37.6711 EndY=0 EndZ=0
    g4: GeomPoint [constr] X=0 Y=101.553 Z=0
    g5: LineSegment StartX=21.7004 StartY=23.9757 StartZ=0 EndX=-14.7224 EndY=47.0077 EndZ=0
    g6: LineSegment StartX=-14.7224 StartY=47.0077 StartZ=0 EndX=12.3269 EndY=62.2732 EndZ=0
    g7: LineSegment StartX=12.3269 StartY=62.2732 StartZ=0 EndX=-17.9362 EndY=82.8949 EndZ=0
    g8: LineSegment StartX=-17.9362 StartY=82.8949 StartZ=0 EndX=15.5406 EndY=105.124 EndZ=0
    g9: LineSegment StartX=15.5406 StartY=105.124 StartZ=0 EndX=-10.7052 EndY=124.674 EndZ=0
    g10: LineSegment StartX=-10.7052 StartY=124.674 StartZ=0 EndX=12.059 EndY=140.743 EndZ=0
  constraints (13):
    c: Coincident(g0,g1)
    c: Coincident(g1,g2)
    c: Coincident(g2,g3)
    c: Coincident(g3,g0)
    c: Horizontal(g0)
    c: PointOnObject(g4,g-2)
    c: Symmetric(g0,g0,g-1)
    c: Symmetric(g1,g2,g-2)
    c: Coincident(g5,g6)
    c: Coincident(g6,g7)
    c: Coincident(g7,g8)
    c: Coincident(g8,g9)
    c: Coincident(g9,g10)
FEATURE [PartDesign::Body] Body001
  AllowCompound = true
  Group = -> [Sketch001]
  Origin = -> Origin001
